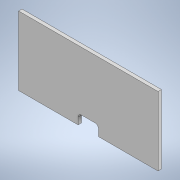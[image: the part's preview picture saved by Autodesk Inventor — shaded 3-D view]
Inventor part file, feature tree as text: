
AUTODESK INVENTOR PART (.ipt)
format: ipt  version: 2021 (Build 250183000, 183)  size: 131,072 bytes
history: native  units: mm
features: extrude x4, sketch x4, fillet x1
ambient origin geometry x8: Origin, YZ Plane, XZ Plane, XY Plane, X Axis, Y Axis, Z Axis, Center Point
bodies: Solid1 (feature_tree)
feature tree (9):
  extrude  "Extrusion1"  Depth=42.5mm
  extrude  "Extrusion2"  Depth=6.0mm
  fillet  "Fillet1"  Radius=12.0mm
  extrude  "Extrusion3"  Depth=86.0mm
  extrude  "Extrusion4"  Depth=2.0mm
  sketch  "Sketch1"  dims[d0=86.0mm d1=42.5mm]
  sketch  "Sketch2"  dims[d2=2.0mm d3=0.0mm d4=6.0mm d5=12.0mm]
  sketch  "Sketch3"  dims[d6=37.0mm d7=86.0mm]
  sketch  "Sketch4"  dims[d8=2.0mm d9=0.0mm d10=2.0mm d11=2.0mm d12=2.0mm d13=0.0mm d14=2.0mm d15=2.0mm d16=2.0mm d17=0.0mm]
